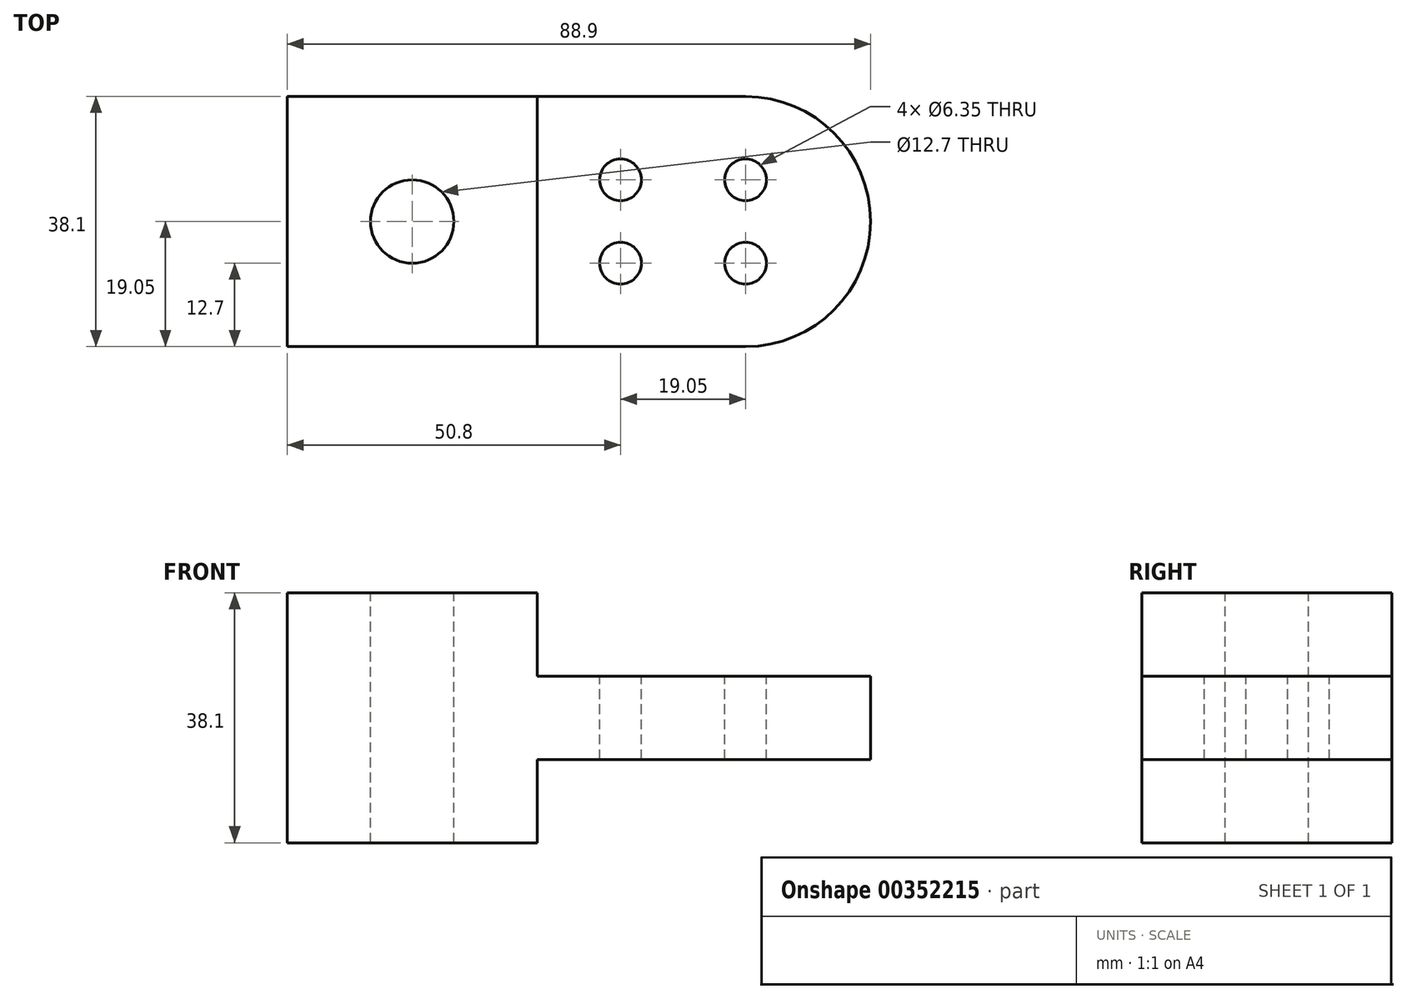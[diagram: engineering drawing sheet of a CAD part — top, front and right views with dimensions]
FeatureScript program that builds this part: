
annotation { "Feature Type Name" : "Feature", "Feature Type Description" : "" }
export const myFeature = defineFeature(function(context is Context, id is Id, definition is map)
    precondition{}
    {
        {
            var Q0;
            Q0=qCreatedBy(makeId("Front.planeOp"),FACE);
            var sketch = newSketch(context, id + "F0", { "sketchPlane" : qUnion([Q0])});
            skLineSegment(sketch, "E0", {"start": v(0, 0) * mm, "end": v(0, 38.1) * mm});
            skLineSegment(sketch, "E1", {"start": v(0, 38.1) * mm, "end": v(38.1, 38.1) * mm});
            skLineSegment(sketch, "E2", {"start": v(38.1, 38.1) * mm, "end": v(38.1, 25.4) * mm});
            skLineSegment(sketch, "E3", {"start": v(38.1, 25.4) * mm, "end": v(88.9, 25.4) * mm});
            skLineSegment(sketch, "E4", {"start": v(88.9, 25.4) * mm, "end": v(88.9, 12.7) * mm});
            skLineSegment(sketch, "E5", {"start": v(88.9, 12.7) * mm, "end": v(38.1, 12.7) * mm});
            skLineSegment(sketch, "E6", {"start": v(38.1, 12.7) * mm, "end": v(38.1, 0) * mm});
            skLineSegment(sketch, "E7", {"start": v(38.1, 0) * mm, "end": v(0, 0) * mm});
            skSolve(sketch);
        }
        {
            var Q0;
            Q0 = qSketchRegion(id + "F0", true);
            extrude(context, id + "F1", {"entities" : qUnion([Q0]), "depth" : 38.1 * mm});
        }
        {
            var Q0;
            Q0=makeQuery(id+"F1.opExtrude","SWEPT_FACE",FACE,{"disambiguationData":[OSD([sQuery(id+"F0.wireOp",EDGE,"E3")])]});
            var sketch = newSketch(context, id + "F2", { "sketchPlane" : qUnion([Q0])});
            skLineSegment(sketch, "E8", {"start": v(69.85, 0) * mm, "end": v(88.9, 0) * mm});
            skLineSegment(sketch, "E9", {"start": v(88.9, 0) * mm, "end": v(88.9, -38.1) * mm});
            skLineSegment(sketch, "E10", {"start": v(88.9, -38.1) * mm, "end": v(69.85, -38.1) * mm});
            skArc(sketch, "E11", {"start": v(69.85, -38.1) * mm, "mid": v(88.9, -19.05) * mm, "end": v(69.85, 0) * mm});
            skSolve(sketch);
        }
        {
            var Q0;
            Q0 = qSketchRegion(id + "F2", true);
            extrude(context, id + "F3", {"entities" : qUnion([Q0]), "operationType" : NewBodyOperationType.REMOVE, "oppositeDirection" : true, "depth" : 25.4 * mm});
        }
        {
            var Q0;
            Q0=makeQuery(id+"F1.opExtrude","SWEPT_FACE",FACE,{"disambiguationData":[OSD([sQuery(id+"F0.wireOp",EDGE,"E3")])]});
            var sketch = newSketch(context, id + "F4", { "sketchPlane" : qUnion([Q0])});
            skCircle(sketch, "E12", {"center": v(50.8, -12.7) * mm, "radius": 3.18 * mm});
            skCircle(sketch, "E13", {"center": v(69.85, -12.7) * mm, "radius": 3.18 * mm});
            skCircle(sketch, "E14", {"center": v(69.85, -25.4) * mm, "radius": 3.18 * mm});
            skCircle(sketch, "E15", {"center": v(50.8, -25.4) * mm, "radius": 3.18 * mm});
            skSolve(sketch);
        }
        {
            var Q0;
            Q0 = qSketchRegion(id + "F4", true);
            extrude(context, id + "F5", {"entities" : qUnion([Q0]), "operationType" : NewBodyOperationType.REMOVE, "endBound" : BoundingType.THROUGH_ALL, "oppositeDirection" : true, "depth" : 25.4 * mm});
        }
        {
            var Q0;
            Q0=makeQuery(id+"F1.opExtrude","SWEPT_FACE",FACE,{"disambiguationData":[OSD([sQuery(id+"F0.wireOp",EDGE,"E1")])]});
            var sketch = newSketch(context, id + "F6", { "sketchPlane" : qUnion([Q0])});
            skCircle(sketch, "E16", {"center": v(19.05, -19.05) * mm, "radius": 6.35 * mm});
            skSolve(sketch);
        }
        {
            var Q0;
            Q0 = qSketchRegion(id + "F6", true);
            extrude(context, id + "F7", {"entities" : qUnion([Q0]), "operationType" : NewBodyOperationType.REMOVE, "endBound" : BoundingType.THROUGH_ALL, "oppositeDirection" : true, "depth" : 25.4 * mm});
        }
    });
